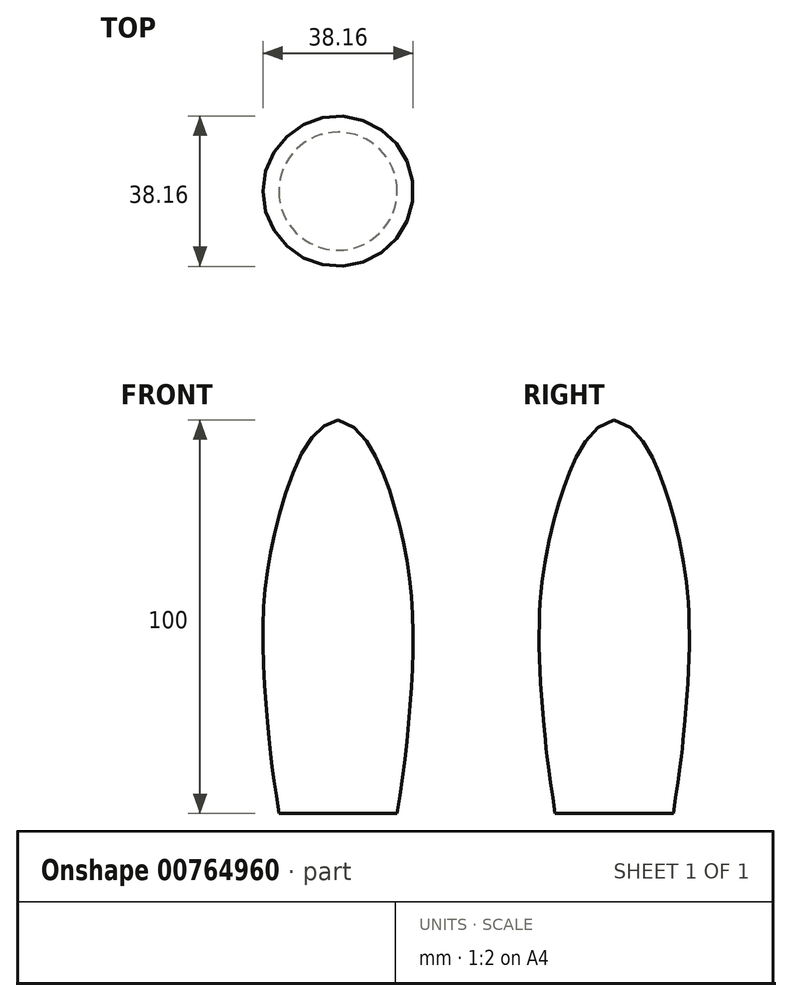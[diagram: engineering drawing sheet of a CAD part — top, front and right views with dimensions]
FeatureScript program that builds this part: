
annotation { "Feature Type Name" : "Feature", "Feature Type Description" : "" }
export const myFeature = defineFeature(function(context is Context, id is Id, definition is map)
    precondition{}
    {
        {
            var Q0;
            Q0=qCreatedBy(makeId("Front.planeOp"),FACE);
            var sketch = newSketch(context, id + "F0", { "sketchPlane" : qUnion([Q0])});
            skLineSegment(sketch, "E0", {"start": v(0, 66.44) * mm, "end": v(0, -33.56) * mm});
            skLineSegment(sketch, "E1", {"start": v(0, -33.56) * mm, "end": v(-15, -33.56) * mm});
            skFitSpline(sketch, "E2", {"points": [v(0, 66.44) * mm, v(-14.8, 42.66) * mm, v(-19.06, 13.83) * mm, v(-17.51, -15) * mm, v(-15, -33.56) * mm], "startDerivative": vector(-87.67, -15.77) * mm, "endDerivative": vector(17.43, -112.32) * mm});
            skSolve(sketch);
        }
        {
            var Q0;
            Q0=makeQuery(id+"F0.imprint","IMPRINT",FACE,{"disambiguationData":[TD([[makeQuery(id+"F0.imprint","IMPRINT",EDGE,{"derivedFrom":sQuery(id+"F0.wireOp",EDGE,"E0")}),-1.0]])]});
            var Q1;
            Q1=sQuery(id+"F0.wireOp",EDGE,"E0");
            revolve(context, id + "F1", {"surfaceOperationType" : NewSurfaceOperationType.NEW, "entities" : qUnion([Q0]), "axis" : qUnion([Q1]), "revolveType" : RevolveType.FULL});
        }
    });
